# Revit family: Quartz_Single_Bowl_Dual_Mount_Sink-Elkay-ELG1616GT0_GS0_MB0_WH0
name_source: partatom
category: Plumbing Fixtures
units: mm (PartAtom-declared; Revit-internal decimal feet)

## family parameters
Cut with Voids When Loaded = No
Host = Face
Maintain Annotation Orientation = No
OmniClass Number = 23.45.05.14.14
OmniClass Title = Sinks/Lavatories
Part Type = Normal
Room Calculation Point = No
Round Connector Dimension = Use Diameter
Shared = No

## types (4) — shared parameters
Approx. Shipping Weight (lbs) = 18
Assembly Code = D2010400
Back Flange = 1.3125 "
Bowl  Dimensions = 13 1/8 inch x 13 1/8 inch x  7 11/16 inch
Bowl Depth = 7.6875 "
Bowl Length = 13.125 "
Bowl Width = 13.125 "
Cutting Length = 15.125 "
Cutting Width = 15.125 "
Default Elevation = 48 "
Description = Lustertone® Classic Stainless Steel 15 3/4 inch x 15 3/4 inch x 7 11/16 inch Single Bowl Dual  Mount Bar Sink
Drain Location = Rear Center
Drain Location Along X- Axis = 6.5625 "
Drain Location Along Y- Axis = 4.125 "
Drain Size = 3.5 "
Front Flange = 1.3125 "
Installation Type = Dual Mount
Left Flange = 1.3125 "
Length of Sink = 15.75 "
Manufacturer = Elkay Manufacturer Company
Manufacturer Brand = Elkay (by Zurn Elkay Water Solutions)
Masking Region for Bowl = 1.05 "
Number of Bowls = 1
Outlet Connection Size (inch) = 1.5 "
Product Documentation Link = https://www.elkayfiles.com
Product Installation Sheet URL = https://www.elkayfiles.com
Product Page URL = https://www.elkay.com
Product Weight (lbs) = 16
Product data URL = https://bimobject.com
Radius for cutting endge = 0.375 "
Repair Parts URL = https://www.elkayfiles.com
Right Flange = 1.3125 "
Sink Depth = 7.6875 "
Sink Dimensions = 15 3/4 inch x 15 3/4 inch x  7 11/16 inch
Type Image = <None>
URL = https://www.elkay.com
Waste Connection = No
Width of Sink = 15.75 "

## per-type parameters (varying)
| type | Main Material | Model |
| ELG1616WH0 (Single Bowl Dual Mount Bar Sink) | Finish-Elkay-White | ELG1616WH0 |
| ELG1616MB0 (Single Bowl Dual Mount Bar Sink) | Finish-Elkay-Matt black | ELG1616MB0 |
| ELG1616GT0 (Single Bowl Dual Mount Bar Sink) | Finish-Elkay-Graphite | ELG1616GT0 |
| ELG1616GS0 (Single Bowl Dual Mount Bar Sink) | Finish-Elkay-Grey stone | ELG1616GS0 |

## geometry (parser evidence)
native form markers: Sweep x5
no freeform markers — native parametric forms only
